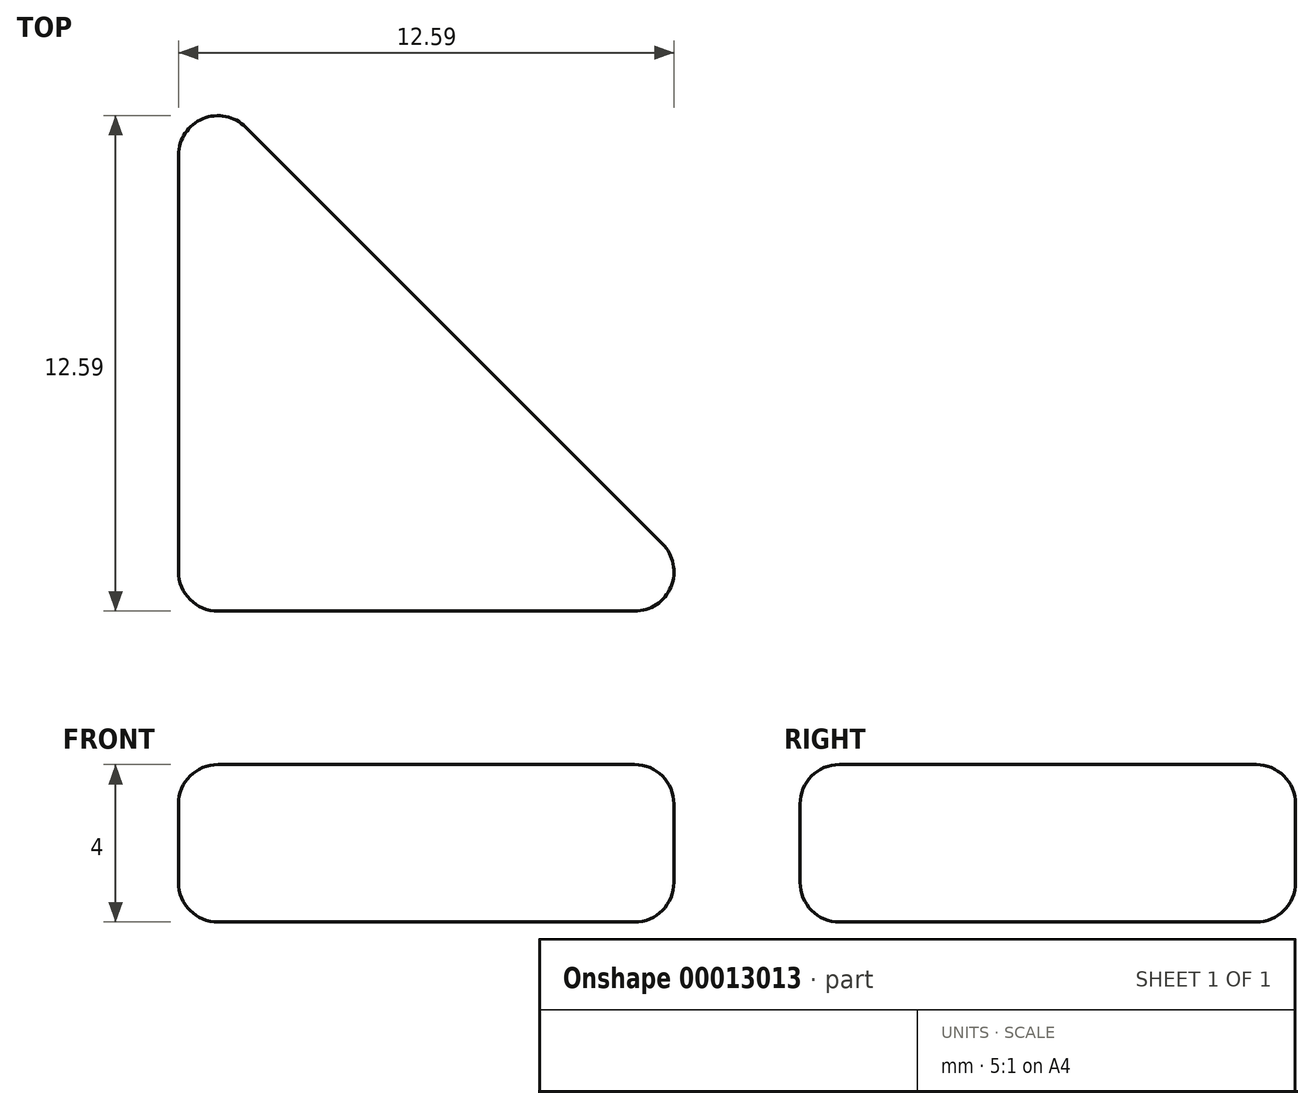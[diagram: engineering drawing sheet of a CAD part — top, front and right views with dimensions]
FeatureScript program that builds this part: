
annotation { "Feature Type Name" : "Feature", "Feature Type Description" : "" }
export const myFeature = defineFeature(function(context is Context, id is Id, definition is map)
    precondition{}
    {
        {
            var Q0;
            Q0=qCreatedBy(makeId("Top.planeOp"),FACE);
            var sketch = newSketch(context, id + "F0", { "sketchPlane" : qUnion([Q0])});
            skLineSegment(sketch, "E0", {"start": v(0, 1) * mm, "end": v(0, 11.59) * mm});
            skLineSegment(sketch, "E1", {"start": v(1.7, 12.3) * mm, "end": v(12.3, 1.7) * mm});
            skLineSegment(sketch, "E2", {"start": v(11.59, 0) * mm, "end": v(1, 0) * mm});
            skPoint(sketch, "E3.visualSharp", {"position": v(0, 14) * mm});
            skArc(sketch, "E3.filletArc", {"start": v(1.7, 12.3) * mm, "mid": v(0.62, 12.5) * mm, "end": v(0, 11.59) * mm});
            skPoint(sketch, "E4.visualSharp", {"position": v(0, 0) * mm});
            skArc(sketch, "E4.filletArc", {"start": v(0, 1) * mm, "mid": v(0.3, 0.3) * mm, "end": v(1, 0) * mm});
            skPoint(sketch, "E5.visualSharp", {"position": v(14, 0) * mm});
            skArc(sketch, "E5.filletArc", {"start": v(11.59, 0) * mm, "mid": v(12.5, 0.62) * mm, "end": v(12.3, 1.7) * mm});
            skSolve(sketch);
        }
        {
            var Q0;
            Q0 = qSketchRegion(id + "F0", true);
            extrude(context, id + "F1", {"entities" : qUnion([Q0]), "depth" : 4 * mm});
        }
        {
            var Q0;
            Q0=makeQuery(id+"F1.opExtrude","CAP_EDGE",EDGE,{"disambiguationData":[OSD([sQuery(id+"F0.wireOp",EDGE,"E2")])],"isStart":false});
            var Q1;
            Q1=makeQuery(id+"F1.opExtrude","CAP_EDGE",EDGE,{"disambiguationData":[OSD([sQuery(id+"F0.wireOp",EDGE,"E2")])],"isStart":true});
            fillet(context, id + "F2", {"entities" : qUnion([Q0, Q1]), "radius" : 1 * mm, "tangentPropagation" : true, "allowEdgeOverflow" : false});
        }
    });
